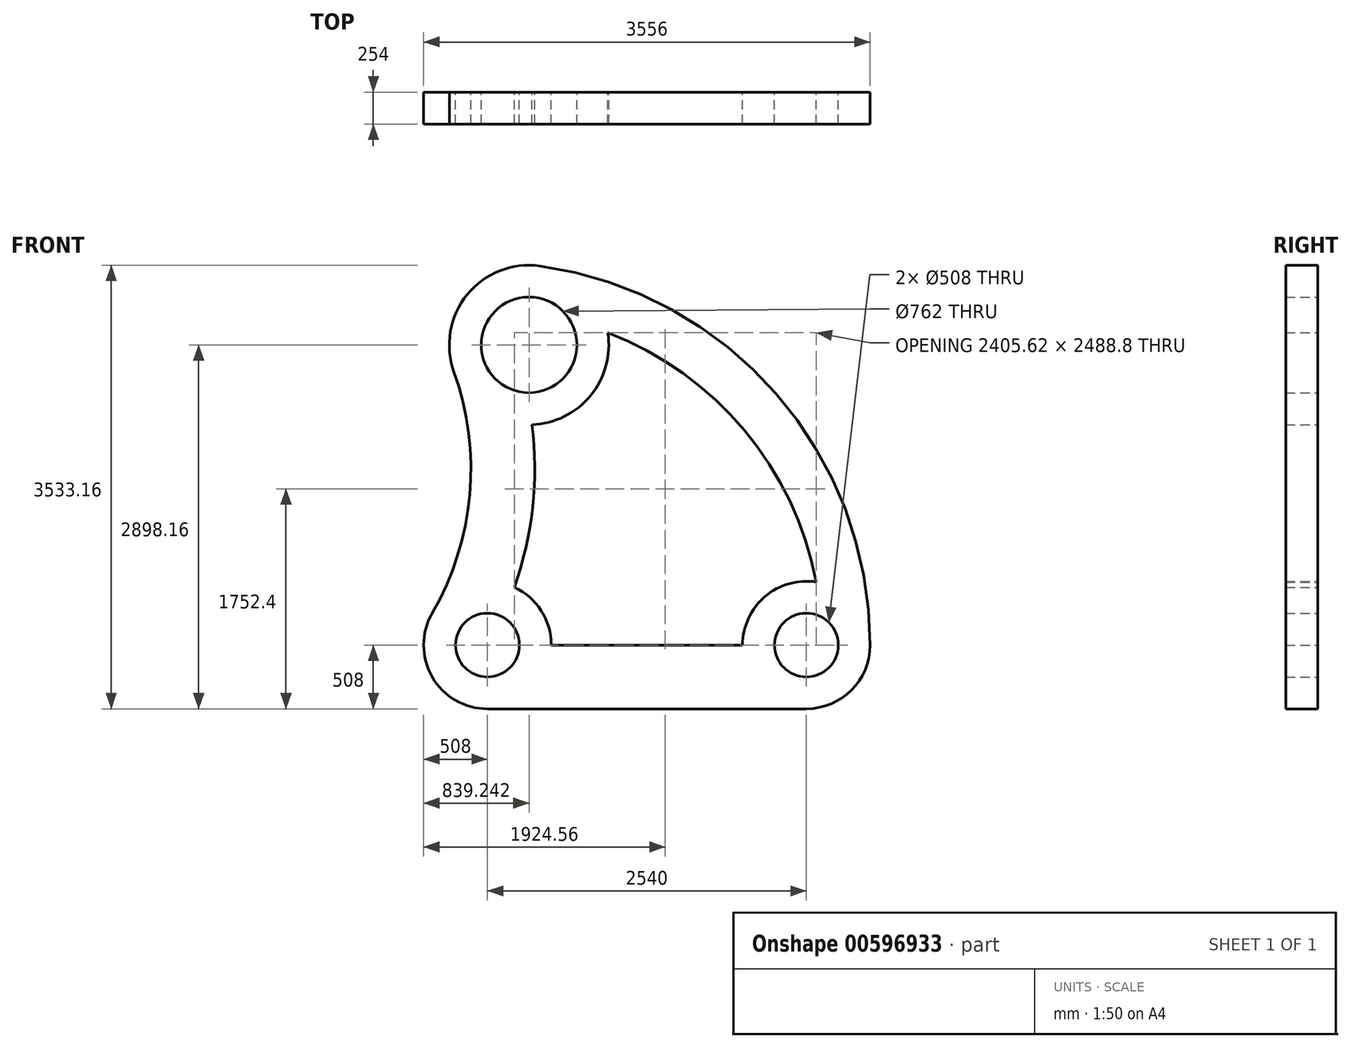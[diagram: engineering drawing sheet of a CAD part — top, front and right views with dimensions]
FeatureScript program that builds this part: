
annotation { "Feature Type Name" : "Feature", "Feature Type Description" : "" }
export const myFeature = defineFeature(function(context is Context, id is Id, definition is map)
    precondition{}
    {
        {
            var Q0;
            Q0=qCreatedBy(makeId("Front.planeOp"),FACE);
            var sketch = newSketch(context, id + "F0", { "sketchPlane" : qUnion([Q0])});
            skCircle(sketch, "E0", {"center": v(0, 0) * mm, "radius": 254 * mm});
            skArc(sketch, "E1", {"start": v(508, 0) * mm, "mid": v(428.17, 273.38) * mm, "end": v(213.75, 460.84) * mm});
            skLineSegment(sketch, "E2", {"start": v(508, 0) * mm, "end": v(2032, 0) * mm});
            skArc(sketch, "E3", {"start": v(2540, -508) * mm, "mid": v(2899.21, -359.21) * mm, "end": v(3048, 0) * mm});
            skCircle(sketch, "E4", {"center": v(2540, 0) * mm, "radius": 254 * mm});
            skLineSegment(sketch, "E5", {"start": v(0, -508) * mm, "end": v(2540, -508) * mm});
            skArc(sketch, "E6", {"start": v(3048, 0) * mm, "mid": v(2298.44, 2001.87) * mm, "end": v(418.41, 3019.14) * mm});
            skArc(sketch, "E7", {"start": v(2619.38, 501.76) * mm, "mid": v(2046.32, 1710.4) * mm, "end": v(958.53, 2488.8) * mm});
            skArc(sketch, "E8.trimOffspring", {"start": v(2619.38, 501.76) * mm, "mid": v(2210.04, 386.26) * mm, "end": v(2032, 0) * mm});
            skCircle(sketch, "E9", {"center": v(331.24, 2390.16) * mm, "radius": 381 * mm});
            skArc(sketch, "E10", {"start": v(354.19, 1755.57) * mm, "mid": v(821.25, 1986.28) * mm, "end": v(958.53, 2488.8) * mm});
            skArc(sketch, "E11", {"start": v(-439.5, 254.76) * mm, "mid": v(-140.5, 1195.8) * mm, "end": v(-266.26, 2175.16) * mm});
            skArc(sketch, "E12.trimOffspring", {"start": v(213.75, 460.84) * mm, "mid": v(360.46, 1099.9) * mm, "end": v(354.19, 1755.57) * mm});
            skArc(sketch, "E13.trimOffspring", {"start": v(418.41, 3019.14) * mm, "mid": v(-161.9, 2790.2) * mm, "end": v(-266.26, 2175.16) * mm});
            skArc(sketch, "E14.trimOffspring", {"start": v(-439.5, 254.76) * mm, "mid": v(-440.16, -253.62) * mm, "end": v(0, -508) * mm});
            skSolve(sketch);
        }
        {
            var Q0;
            Q0=makeQuery(id+"F0.imprint","IMPRINT",FACE,{"disambiguationData":[TD([[makeQuery(id+"F0.imprint","IMPRINT",EDGE,{"derivedFrom":sQuery(id+"F0.wireOp",EDGE,"E0")}),-1.0]])]});
            extrude(context, id + "F1", {"entities" : qUnion([Q0]), "depth" : 254 * mm, "offsetDistance" : 25.4 * mm});
        }
    });
